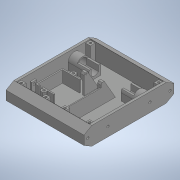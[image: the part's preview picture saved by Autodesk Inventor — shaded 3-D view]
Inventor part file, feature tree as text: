
AUTODESK INVENTOR PART (.ipt)
format: ipt  version: 2020 (Build 240168000, 168)  size: 607,232 bytes
history: native  units: in
note: dims shown in document units (in); Inventor stores cm internally (conversion verified against a paired STEP export)
features: extrude x18, sketch x17, projected_geometry x14, mirror x6, plane x1
ambient origin geometry x8: Origin, YZ Plane, XZ Plane, XY Plane, X Axis, Y Axis, Z Axis, Center Point
bodies: Solid1 (feature_tree)
feature tree (56):
  extrude  "Extrusion1"  Depth=5.9055in
  extrude  "Extrusion2"  TaperAngle=0.0deg  [1 undecoded]
  extrude  "Extrusion3"  Depth=1.063in
  extrude  "Extrusion4"  Depth=0.315in
  extrude  "Extrusion5"  TaperAngle=0.0deg  [1 undecoded]
  extrude  "Extrusion6"  Depth=0.5906in
  mirror  "Mirror1"
  extrude  "Extrusion7"  Depth=0.0787in
  mirror  "Mirror2"
  extrude  "Extrusion8"  Depth=0.6102in
  mirror  "Mirror3"
  plane  "Work Plane1"
  extrude  "Extrusion9"  Depth=0.7874in TaperAngle=0.0deg
  mirror  "Mirror4"
  extrude  "Extrusion10"  Depth=6.063in TaperAngle=0.0deg
  extrude  "Extrusion11"  Depth=0.1575in
  extrude  "Extrusion12"  TaperAngle=0.0deg  [1 undecoded]
  extrude  "Extrusion13"  Depth=0.2756in
  extrude  "Extrusion14"  Depth=0.4331in
  extrude  "Extrusion17"  Depth=2.7559in
  extrude  "Extrusion18"  Depth=0.0413in
  mirror  "Mirror6"
  extrude  "Extrusion19"  TaperAngle=0.0deg  [1 undecoded]
  mirror  "Mirror7"
  extrude  "Extrusion20"  TaperAngle=60.0deg  [1 undecoded]
  sketch  "Sketch1"  dims[d0=1.1811in d1=5.9055in]
  sketch  "Sketch2"  dims[d2=5.1181in d3=0.0in]
  projected_geometry  "Projected Loop1"
  sketch  "Sketch3"  dims[d4=0.1575in d5=1.063in]
  projected_geometry  "Projected Loop2"
  projected_geometry  "Projected Loop3"
  sketch  "Sketch4"  dims[d6=0.0in d8=0.315in]
  projected_geometry  "Projected Loop4"
  sketch  "Sketch6"  dims[d10=0.993in d11=0.0in]
  sketch  "Sketch7"  dims[d12=0.6496in d13=0.5906in]
  sketch  "Sketch9"  dims[d14=1.5748in d15=0.0787in]
  sketch  "Sketch10"  dims[d16=0.5512in d17=0.0in d18=0.6102in]
  sketch  "Sketch12"  dims[d19=0.4803in d20=0.7874in d21=0.0in]
  projected_geometry  "Projected Loop6"
  projected_geometry  "Projected Loop7"
  projected_geometry  "Projected Loop8"
  sketch  "Sketch13"  dims[d22=0.1654in d23=6.063in d24=0.0in]
  sketch  "Sketch14"  dims[d25=0.5114in d26=0.1575in]
  sketch  "Sketch15"  dims[d27=1.5748in d28=0.0in d29=0.0in]
  projected_geometry  "Projected Loop15"
  sketch  "Sketch16"  dims[d30=0.1575in d31=0.2756in]
  projected_geometry  "Projected Loop19"
  projected_geometry  "Projected Loop20"
  projected_geometry  "Projected Loop21"
  projected_geometry  "Projected Loop22"
  projected_geometry  "Projected Loop23"
  projected_geometry  "Projected Loop24"
  sketch  "Sketch20"  dims[d32=0.0in d33=0.4331in]
  sketch  "Sketch21"  dims[d34=0.0827in d38=2.7559in]
  sketch  "Sketch22"  dims[d40=0.0413in d41=0.0909in]
  sketch  "Sketch23"  dims[d42=0.2362in d43=0.0in d44=60.0deg d45=0.0787in d46=0.315in d48=0.993in d49=0.0in d53=0.2756in d54=0.0in d55=0.4724in d56=1.2008in d57=1.6142in d58=1.5945in d59=0.0787in d60=0.0787in d62=0.315in d63=0.7677in d64=0.0in d66=0.1476in d67=0.2756in d68=0.0in d69=0.7874in d70=0.2953in d71=0.1181in d72=0.0in d89=0.0157in d90=0.0157in d91=0.1476in d92=0.1476in d96=0.315in d97=0.1575in d98=0.1181in d99=0.0in d102=0.1772in d104=0.3346in d105=135.0deg d106=0.2362in d107=0.0in d108=0.0394in d109=0.0in d110=0.063in d111=0.0394in d112=0.0in]
note: 5 required parameter values undecoded (feature->parameter linkage not recoverable at this tier; creation-order binding heuristic only, values carry confidence <= 0.55)
